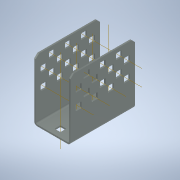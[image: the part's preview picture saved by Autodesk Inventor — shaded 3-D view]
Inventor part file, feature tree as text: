
AUTODESK INVENTOR PART (.ipt)
format: ipt  version: 2020 (Build 240168000, 168)  size: 710,144 bytes
history: native  units: in
note: dims shown in document units (in); Inventor stores cm internally (conversion verified against a paired STEP export)
features: other x55, extrude x32, sketch x9, sheet_metal_op x3, pattern_linear x3, plane x2, mirror x2
ambient origin geometry x8: Origin, YZ Plane, XZ Plane, XY Plane, X Axis, Y Axis, Z Axis, Center Point
bodies: Solid1 (feature_tree)
feature tree (106):
  sheet_metal_op  "Face1"
  sheet_metal_op  "Flange1"
  other  "Corner Chamfer1"
  plane  "Work Plane1"
  mirror  "Mirror1"
  pattern_linear  "Rectangular Pattern1"  Spacing1=0.047in  [1 undecoded]
  pattern_linear  "Rectangular Pattern2"  Spacing1=0.047in  [1 undecoded]
  plane  "Work Plane2"
  mirror  "Mirror2"
  pattern_linear  "Rectangular Pattern3"  Spacing1=0.1in  [1 undecoded]
  sketch  "Sketch8"  dims[d7=1.885in d8=90.0deg d9=0.047in]
  other  "Work Axis1"
  other  "Work Axis2"
  other  "Work Axis3"
  other  "Work Axis4"
  other  "Work Axis5"
  other  "Work Axis6"
  other  "Work Axis7"
  other  "Work Axis8"
  other  "Work Axis9"
  other  "Work Axis10"
  other  "Work Axis11"
  other  "Work Axis12"
  other  "Work Axis13"
  other  "Work Axis14"
  sketch  "Sketch9"  dims[d10=0.188in d11=0.047in d12=0.047in d13=0.1in d14=0.25in d15=45.0deg d16=0.182in d17=0.182in d18=0.02in d19=0.5in d20=0.206in d21=1.1811in d23=0.5in d24=0.3937in d26=1.0in d28=0.7874in d30=0.5in d31=0.3937in d33=1.0in d35=0.02in d36=0.25in d37=0.182in d38=0.182in d39=0.25in d40=1.5748in d42=0.5in d43=0.7874in d45=0.5in d48=0.047in d49=0.0in d50=0.182in d51=0.182in d52=0.02in d53=0.25in d54=1.5748in d56=0.5in d57=0.3937in d59=1.0in d61=0.047in d62=0.0in d63=1.0in d64=0.0in d65=1.1811in d67=0.5in d68=0.7874in d70=0.5in d71=1.0in d72=0.0in d73=1.5748in d75=0.5in d76=0.7874in d78=0.5in d79=1.0in d80=0.0in d81=1.5748in d83=0.5in d84=0.0in d85=0.0in d86=0.0in d87=0.0in d88=0.0in d89=0.0in d90=0.0in d91=0.0in d92=0.0in d93=0.0in d94=0.0in d95=0.0in d96=0.0in d97=0.0in d98=0.0in d99=0.0in d100=0.0in d101=0.0in d102=0.0in d103=0.0in d104=0.0in d105=0.0in d106=0.0in d107=0.0in d108=0.0in d109=0.0in d110=0.0in d111=0.0in d112=0.0in d113=0.0in d114=0.0in d115=0.0in d116=0.0in d117=0.0in d118=0.0in d119=0.0in d120=0.0in d121=0.0in d122=0.0in d123=0.0in d124=0.0in d125=0.0in d126=0.0in d127=0.0in d128=0.0in d129=0.0in d130=0.0in d131=0.0in d132=0.0in d133=0.0in d134=0.0in d135=0.0in d136=0.0in d137=0.0in d138=0.0in d139=0.0in d140=0.0in d141=0.0in d142=0.0in d143=0.0in d144=0.0in d145=0.0in d146=0.0in d147=0.0in d148=0.047in]
  other  "Work Axis15"
  other  "Work Axis16"
  other  "Work Axis18"
  other  "Work Axis19"
  sketch  "Sketch1"  dims[d0=2.0in]
  other  "Plate1"
  sketch  "Sketch2"  dims[d1=1.129in]
  other  "Plate2"
  sheet_metal_op  "Bend1"
  sketch  "Sketch3"  dims[d2=0.047in]
  sketch  "Sketch4"  dims[d3=0.047in]
  sketch  "Sketch5"  dims[d4=0.0235in]
  other  "Srf1"
  other  "Srf2"
  other  "Srf3"
  other  "Srf4"
  other  "Srf5"
  other  "Srf6"
  sketch  "Sketch6"  dims[d5=0.094in]
  other  "Srf7"
  other  "Srf8"
  other  "Srf9"
  other  "Srf10"
  other  "Srf11"
  other  "Srf12"
  other  "Srf13"
  other  "Srf14"
  other  "Srf18"
  other  "Srf19"
  other  "Srf20"
  other  "Srf15"
  other  "Srf16"
  other  "Srf17"
  other  "Srf21"
  other  "Srf22"
  other  "Srf23"
  other  "Srf24"
  other  "Srf25"
  other  "Srf26"
  other  "Srf27"
  other  "Srf28"
  sketch  "Sketch7"  dims[d6=0.047in]
  other  "Srf29"
  other  "Srf30"
  other  "Srf31"
  other  "Srf32"
  other  "Cut1"
  other  "Cut2"
  extrude  "ExtrusionSrf1"  Depth=0.182in
  extrude  "ExtrusionSrf7"  Depth=0.182in
  extrude  "ExtrusionSrf29"  Depth=0.02in
  extrude  "ExtrusionSrf2"  Depth=0.5in
  extrude  "ExtrusionSrf3"  Depth=0.047in
  extrude  "ExtrusionSrf4"  Depth=0.5in
  extrude  "ExtrusionSrf5"  Depth=0.5in
  extrude  "ExtrusionSrf6"  Depth=0.02in
  extrude  "ExtrusionSrf8"  Depth=0.25in
  extrude  "ExtrusionSrf9"  Depth=0.182in
  extrude  "ExtrusionSrf10"  Depth=0.182in
  extrude  "ExtrusionSrf11"  Depth=0.25in
  extrude  "ExtrusionSrf12"  Depth=0.5in
  extrude  "ExtrusionSrf13"  Depth=0.047in
  extrude  "ExtrusionSrf14"  TaperAngle=0.0deg  [1 undecoded]
  extrude  "ExtrusionSrf15"  Depth=0.182in
  extrude  "ExtrusionSrf16"  Depth=0.182in
  extrude  "ExtrusionSrf17"  Depth=0.02in
  extrude  "ExtrusionSrf18"  Depth=0.25in
  extrude  "ExtrusionSrf19"  Depth=0.5in
  extrude  "ExtrusionSrf20"  Depth=0.047in
  extrude  "ExtrusionSrf21"  TaperAngle=0.0deg  [1 undecoded]
  extrude  "ExtrusionSrf22"  Depth=1.0in TaperAngle=0.0deg
  extrude  "ExtrusionSrf23"  Depth=0.5in
  extrude  "ExtrusionSrf24"  Depth=0.5in
  extrude  "ExtrusionSrf25"  Depth=1.0in TaperAngle=0.0deg
  extrude  "ExtrusionSrf26"  Depth=0.5in
  extrude  "ExtrusionSrf27"  Depth=0.5in
  extrude  "ExtrusionSrf28"  Depth=1.0in TaperAngle=0.0deg
  extrude  "ExtrusionSrf30"  Depth=0.5in
  extrude  "ExtrusionSrf31"  TaperAngle=0.0deg  [1 undecoded]
  extrude  "ExtrusionSrf32"  TaperAngle=0.0deg  [1 undecoded]
note: 7 required parameter values undecoded (feature->parameter linkage not recoverable at this tier; creation-order binding heuristic only, values carry confidence <= 0.55)
